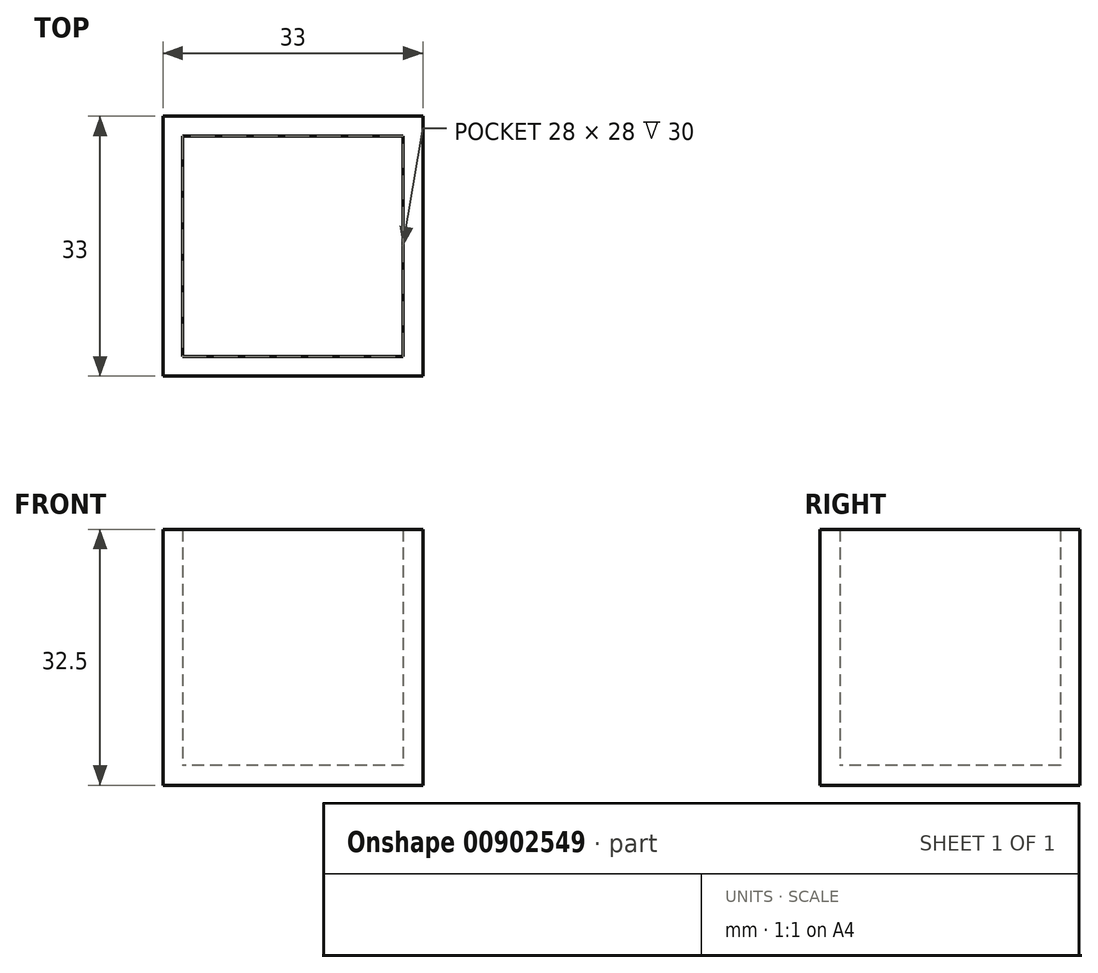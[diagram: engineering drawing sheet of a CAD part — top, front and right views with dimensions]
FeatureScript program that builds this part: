
annotation { "Feature Type Name" : "Feature", "Feature Type Description" : "" }
export const myFeature = defineFeature(function(context is Context, id is Id, definition is map)
    precondition{}
    {
        {
            var Q0;
            Q0=qCreatedBy(makeId("Top.planeOp"),FACE);
            var sketch = newSketch(context, id + "F0", { "sketchPlane" : qUnion([Q0])});
            skLineSegment(sketch, "E0.bottom", {"start": v(14, 14) * mm, "end": v(-14, 14) * mm});
            skLineSegment(sketch, "E0.top", {"start": v(14, -14) * mm, "end": v(-14, -14) * mm});
            skLineSegment(sketch, "E0.left", {"start": v(14, 14) * mm, "end": v(14, -14) * mm});
            skLineSegment(sketch, "E0.right", {"start": v(-14, 14) * mm, "end": v(-14, -14) * mm});
            skPoint(sketch, "E0.middle", {"position": v(0, 0) * mm});
            skLineSegment(sketch, "E1.bottom", {"start": v(16.5, 16.5) * mm, "end": v(-16.5, 16.5) * mm});
            skLineSegment(sketch, "E1.top", {"start": v(16.5, -16.5) * mm, "end": v(-16.5, -16.5) * mm});
            skLineSegment(sketch, "E1.left", {"start": v(16.5, 16.5) * mm, "end": v(16.5, -16.5) * mm});
            skLineSegment(sketch, "E1.right", {"start": v(-16.5, 16.5) * mm, "end": v(-16.5, -16.5) * mm});
            skSolve(sketch);
        }
        {
            var Q0;
            Q0=makeQuery(id+"F0.imprint","IMPRINT",FACE,{"disambiguationData":[TD([[makeQuery(id+"F0.imprint","IMPRINT",EDGE,{"derivedFrom":sQuery(id+"F0.wireOp",EDGE,"E0.bottom")}),-1.0]])]});
            var Q1;
            Q1=makeQuery(id+"F0.imprint","IMPRINT",FACE,{"disambiguationData":[TD([[makeQuery(id+"F0.imprint","IMPRINT",EDGE,{"derivedFrom":sQuery(id+"F0.wireOp",EDGE,"E0.bottom")}),1.0]])]});
            extrude(context, id + "F1", {"entities" : qUnion([Q0, Q1]), "oppositeDirection" : true, "depth" : 2.5 * mm, "offsetDistance" : 25 * mm});
        }
        {
            var Q0;
            Q0=makeQuery(id+"F0.imprint","IMPRINT",FACE,{"disambiguationData":[TD([[makeQuery(id+"F0.imprint","IMPRINT",EDGE,{"derivedFrom":sQuery(id+"F0.wireOp",EDGE,"E0.bottom")}),-1.0]])]});
            extrude(context, id + "F2", {"entities" : qUnion([Q0]), "operationType" : NewBodyOperationType.ADD, "depth" : 30 * mm, "offsetDistance" : 25 * mm});
        }
    });
